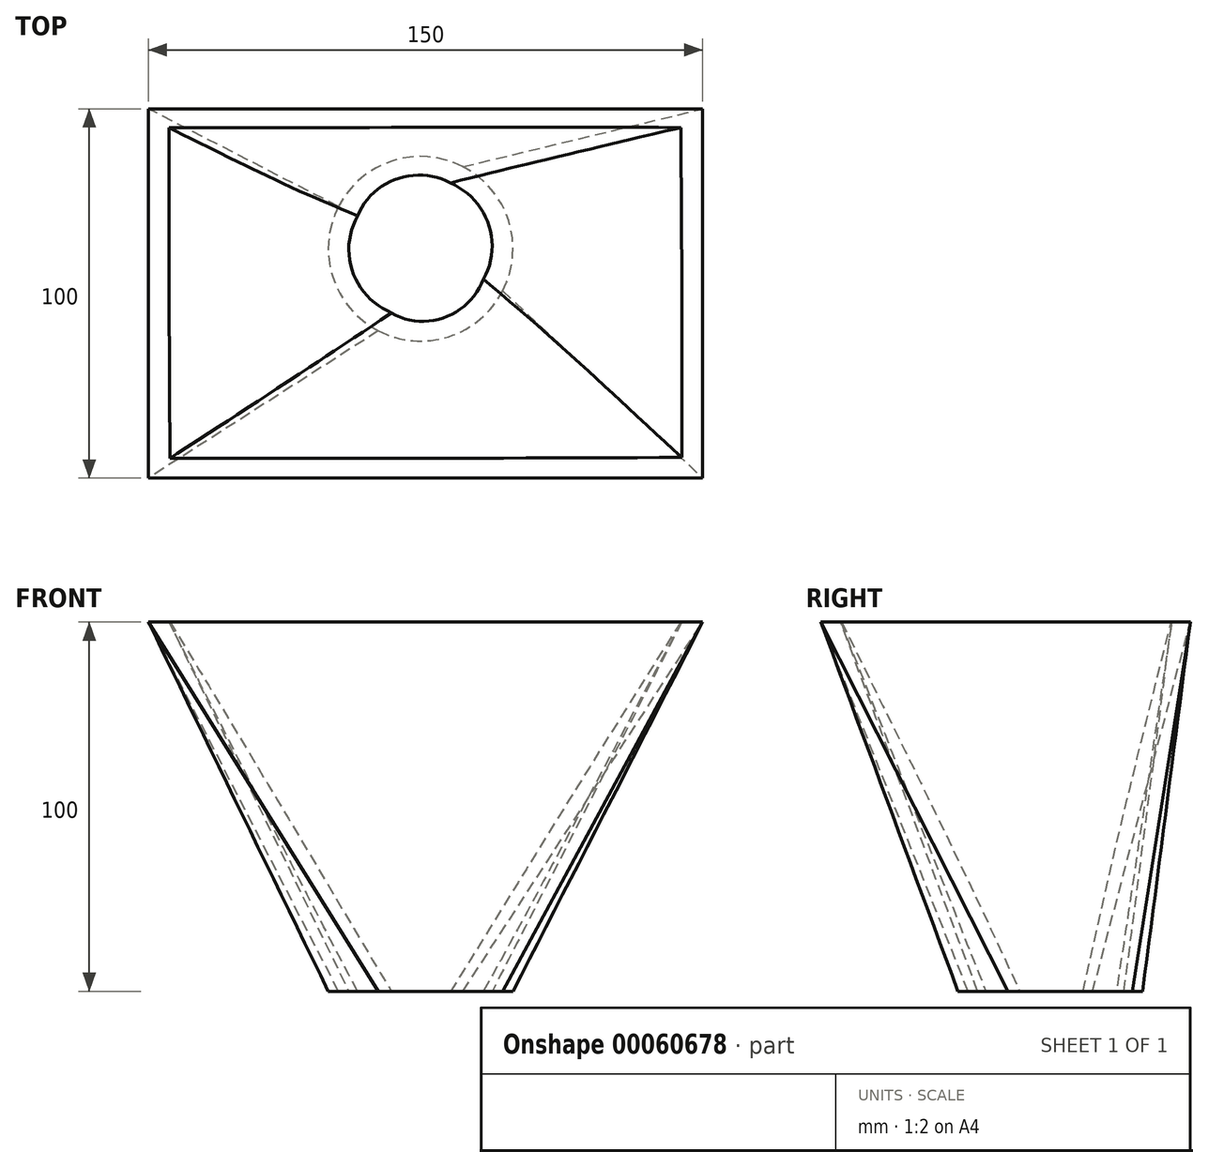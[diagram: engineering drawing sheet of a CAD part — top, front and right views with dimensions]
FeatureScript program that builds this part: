
annotation { "Feature Type Name" : "Feature", "Feature Type Description" : "" }
export const myFeature = defineFeature(function(context is Context, id is Id, definition is map)
    precondition{}
    {
        {
            var Q0;
            Q0=qCreatedBy(makeId("Top.planeOp"),FACE);
            var sketch = newSketch(context, id + "F0", { "sketchPlane" : qUnion([Q0])});
            skCircle(sketch, "E0", {"center": v(0, 0) * mm, "radius": 25 * mm});
            skSolve(sketch);
        }
        {
            var Q0;
            Q0=qCreatedBy(makeId("Top.planeOp"),FACE);
            cPlane(context, id + "F1", {"entities" : qUnion([Q0]), "cplaneType" : CPlaneType.OFFSET, "offset" : 100 * mm, "width" : 150 * mm, "height" : 150 * mm});
        }
        {
            var Q0;
            Q0=qCreatedBy(id+"F1.planeOp",FACE);
            var sketch = newSketch(context, id + "F2", { "sketchPlane" : qUnion([Q0])});
            skLineSegment(sketch, "E1.bottom", {"start": v(-73.66, 37.9) * mm, "end": v(76.34, 37.9) * mm});
            skLineSegment(sketch, "E1.top", {"start": v(-73.66, -62.1) * mm, "end": v(76.34, -62.1) * mm});
            skLineSegment(sketch, "E1.left", {"start": v(-73.66, 37.9) * mm, "end": v(-73.66, -62.1) * mm});
            skLineSegment(sketch, "E1.right", {"start": v(76.34, 37.9) * mm, "end": v(76.34, -62.1) * mm});
            skSolve(sketch);
        }
        {
            var Q0;
            Q0=makeQuery(id+"F0.imprint","IMPRINT",FACE,{"disambiguationData":[TD([[makeQuery(id+"F0.imprint","IMPRINT",EDGE,{"derivedFrom":sQuery(id+"F0.wireOp",EDGE,"E0")}),1.0]])]});
            var Q1;
            Q1=makeQuery(id+"F2.imprint","IMPRINT",FACE,{"disambiguationData":[TD([[makeQuery(id+"F2.imprint","IMPRINT",EDGE,{"derivedFrom":sQuery(id+"F2.wireOp",EDGE,"E1.bottom")}),-1.0]])]});
            loft(context, id + "F3", {"sheetProfilesArray" : [{ "sheetProfileEntities" : qUnion([Q0]) }, { "sheetProfileEntities" : qUnion([Q1]) }]});
        }
        {
            var Q0;
            Q0=makeQuery(id+"F3.opLoft","CAP_FACE",FACE,{"disambiguationData":[OSD([makeQuery(id+"F0.imprint","IMPRINT",FACE,{"disambiguationData":[TD([[makeQuery(id+"F0.imprint","IMPRINT",EDGE,{"derivedFrom":sQuery(id+"F0.wireOp",EDGE,"E0")}),1.0]])]})])],"isStart":true});
            var Q1;
            Q1=makeQuery(id+"F3.opLoft","CAP_FACE",FACE,{"disambiguationData":[OSD([makeQuery(id+"F2.imprint","IMPRINT",FACE,{"disambiguationData":[TD([[makeQuery(id+"F2.imprint","IMPRINT",EDGE,{"derivedFrom":sQuery(id+"F2.wireOp",EDGE,"E1.bottom")}),-1.0]])]})])],"isStart":true});
            shell(context, id + "F4", {"entities" : qUnion([Q0, Q1]), "thickness" : 5 * mm});
        }
    });
